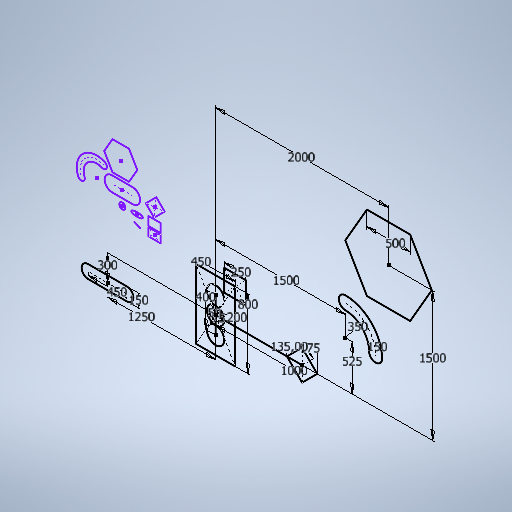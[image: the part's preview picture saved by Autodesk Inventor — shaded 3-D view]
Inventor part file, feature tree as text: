
AUTODESK INVENTOR PART (.ipt)
format: ipt  version: 2025.2 (Build 292293000, 293)  size: 308,224 bytes
history: native  units: mm
features: sketch x1
ambient origin geometry x8: Origin, YZ Plane, XZ Plane, XY Plane, X Axis, Y Axis, Z Axis, Center Point
feature tree (1):
  sketch  "Esboço1"  dims[d0=400.0mm d1=200.0mm d2=75.0mm d3=50.0mm d4=450.0mm d5=800.0mm d6=250.0mm d7=1000.0mm d8=175.0mm d9=135.0deg d10=450.0mm d11=300.0mm d12=1250.0mm d13=150.0mm d14=1500.0mm d15=525.0mm d16=350.0mm d17=150.0mm d18=2000.0mm d19=1500.0mm d20=500.0mm]
